# Revit family: Toilet_Seat-Round_Closed_Front-KOHLER-Cachet_Quick-Release-K-7316
name_source: partatom
category: Specialty Equipment
revit_build: Autodesk Revit 2017 (Build: 20160225_1515(x64)
units: mm (PartAtom-declared; Revit-internal decimal feet)

## family parameters
Cut with Voids When Loaded = No
Host = Face
OmniClass Number = 23.31.19.19.17
OmniClass Title = Water Closet Seats
Part Type = Normal
Room Calculation Point = No
Round Connector Dimension = Use Diameter
Shared = No

## types (6) — shared parameters
ADA Compliant = No
Assembly Code = C1030200
Date Modified = 02/09/2021
Description = Round-front toilet seat
Height = 1"
Length = 16 1/16"
Manufacturer = KOHLER Co.
Master Format 2014 = 10 28 00
Master Format 2014 Name = Toilet, Bath, and Laundry Accessories
Material = Plastic
Product Documentation Link = https://www.us.kohler.com
Product Name = Cachet_Quick-Release
Product Page URL = http://www.us.kohler.com
URL = https://www.us.kohler.com
WaterSense Certified = No
Width = 14 3/16"

## per-type parameters (varying)
| type | Default Elevation | Finish | Model | Type |
| 0-White | 0" | Kohler-Plastic-0-White | K-7316-0 | 1 |
| 96-Biscuit | 42" | Kohler-Plastic-96-Biscuit | K-7316-96 | 2 |
| NY-Dune | 42" | Kohler-Plastic-NY-Dune | K-7316-NY | 3 |
| 95-Ice Grey | 42" | Kohler-Plastic-95-Ice_Grey | K-7316-95 | 4 |
| G9-Sandbar | 42" | Kohler-Plastic-G9-Sandbar | K-7316-G9 | 5 |
| 7-Black Black | 42" | Kohler-Plastic-7-Black_Black | K-7316-7 | 6 |

## geometry (parser evidence)
native form markers: Sweep x5
no freeform markers — native parametric forms only
